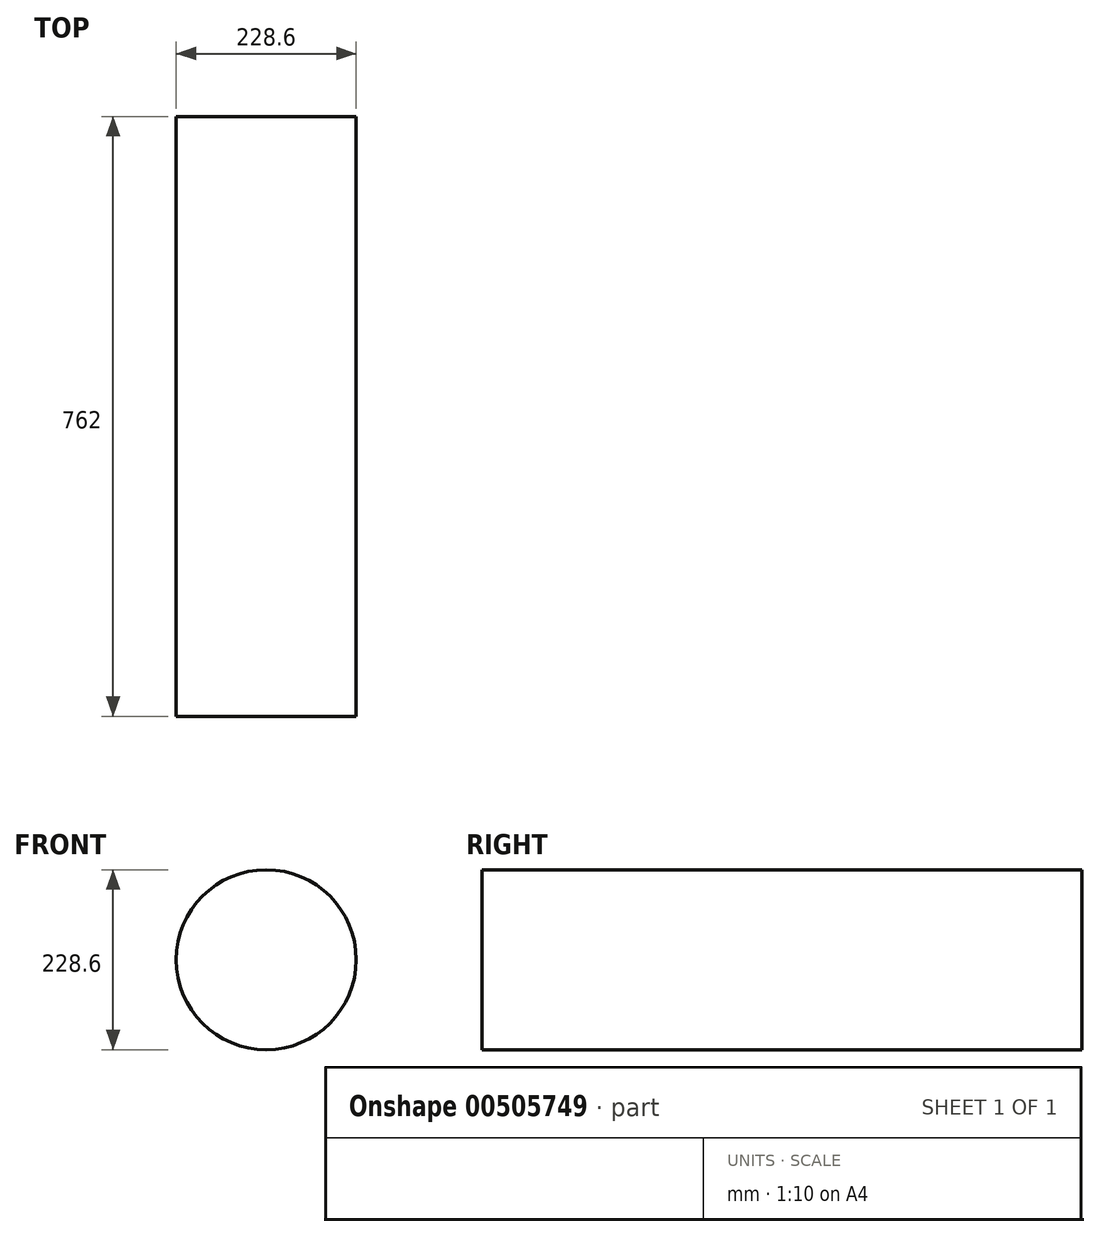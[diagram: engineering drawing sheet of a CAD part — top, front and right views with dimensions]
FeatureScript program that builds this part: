
annotation { "Feature Type Name" : "Feature", "Feature Type Description" : "" }
export const myFeature = defineFeature(function(context is Context, id is Id, definition is map)
    precondition{}
    {
        {
            var Q0;
            Q0=qCreatedBy(makeId("Top.planeOp"),FACE);
            var sketch = newSketch(context, id + "F0", { "sketchPlane" : qUnion([Q0])});
            skLineSegment(sketch, "E0.left", {"start": v(-1447.8, 381) * mm, "end": v(-1447.8, -381) * mm});
            skPoint(sketch, "E0.middle", {"position": v(0, 0) * mm});
            skLineSegment(sketch, "E1.left", {"start": v(-114.3, 381) * mm, "end": v(-114.3, -381) * mm});
            skLineSegment(sketch, "E2.bottom", {"start": v(-1441.45, 381) * mm, "end": v(-1428.75, 381) * mm});
            skLineSegment(sketch, "E2.top", {"start": v(-1441.45, -381) * mm, "end": v(-1428.75, -381) * mm});
            skLineSegment(sketch, "E2.left", {"start": v(-1447.8, 374.65) * mm, "end": v(-1447.8, -374.65) * mm});
            skLineSegment(sketch, "E2.right", {"start": v(-1428.75, 381) * mm, "end": v(-1428.75, -381) * mm});
            skLineSegment(sketch, "E3.bottom", {"start": v(-1428.75, 381) * mm, "end": v(-1162.05, 381) * mm});
            skLineSegment(sketch, "E3.top", {"start": v(-1428.75, -381) * mm, "end": v(-1162.05, -381) * mm});
            skLineSegment(sketch, "E3.right", {"start": v(-1162.05, 381) * mm, "end": v(-1162.05, -381) * mm});
            skLineSegment(sketch, "E4.bottom", {"start": v(-1162.05, 381) * mm, "end": v(-1143, 381) * mm});
            skLineSegment(sketch, "E4.top", {"start": v(-1162.05, -381) * mm, "end": v(-1143, -381) * mm});
            skLineSegment(sketch, "E4.right", {"start": v(-1143, 381) * mm, "end": v(-1143, -381) * mm});
            skLineSegment(sketch, "E5.right", {"start": v(-876.3, 381) * mm, "end": v(-876.3, -381) * mm});
            skLineSegment(sketch, "E6.right", {"start": v(-857.25, 381) * mm, "end": v(-857.25, -381) * mm});
            skLineSegment(sketch, "E7.right", {"start": v(-590.55, 381) * mm, "end": v(-590.55, -381) * mm});
            skLineSegment(sketch, "E8.right", {"start": v(-571.5, 381) * mm, "end": v(-571.5, -381) * mm});
            skLineSegment(sketch, "E9.right", {"start": v(-304.8, 381) * mm, "end": v(-304.8, -381) * mm});
            skLineSegment(sketch, "E10.right", {"start": v(-285.75, 381) * mm, "end": v(-285.75, -381) * mm});
            skPoint(sketch, "E11.visualSharp", {"position": v(-1447.8, 381) * mm});
            skArc(sketch, "E11.filletArc", {"start": v(-1441.45, 381) * mm, "mid": v(-1445.94, 379.14) * mm, "end": v(-1447.8, 374.65) * mm});
            skPoint(sketch, "E12.visualSharp", {"position": v(-1447.8, -381) * mm});
            skArc(sketch, "E12.filletArc", {"start": v(-1447.8, -374.65) * mm, "mid": v(-1445.94, -379.14) * mm, "end": v(-1441.45, -381) * mm});
            skLineSegment(sketch, "E13", {"start": v(0, 381) * mm, "end": v(0, -381) * mm});
            skLineSegment(sketch, "E14", {"start": v(-1447.8, 0) * mm, "end": v(0, 0) * mm});
            skLineSegment(sketch, "E15", {"start": v(-1447.8, 381) * mm, "end": v(0, 381) * mm});
            skLineSegment(sketch, "E16", {"start": v(0, -381) * mm, "end": v(-1447.8, -381) * mm});
            skLineSegment(sketch, "E17.MirrorCS", {"start": v(1441.45, 381) * mm, "end": v(1428.75, 381) * mm});
            skLineSegment(sketch, "E18.MirrorCS", {"start": v(1441.45, -381) * mm, "end": v(1428.75, -381) * mm});
            skArc(sketch, "E19.MirrorCS", {"start": v(1447.8, -374.65) * mm, "mid": v(1445.94, -379.14) * mm, "end": v(1441.45, -381) * mm});
            skArc(sketch, "E20.MirrorCS", {"start": v(1441.45, 381) * mm, "mid": v(1445.94, 379.14) * mm, "end": v(1447.8, 374.65) * mm});
            skLineSegment(sketch, "E21.MirrorCS", {"start": v(1162.05, 381) * mm, "end": v(1143, 381) * mm});
            skLineSegment(sketch, "E22.MirrorCS", {"start": v(1162.05, -381) * mm, "end": v(1143, -381) * mm});
            skLineSegment(sketch, "E23.MirrorCS", {"start": v(1428.75, 381) * mm, "end": v(1162.05, 381) * mm});
            skLineSegment(sketch, "E24.MirrorCS", {"start": v(876.3, 381) * mm, "end": v(876.3, -381) * mm});
            skLineSegment(sketch, "E25.MirrorCS", {"start": v(1447.8, 381) * mm, "end": v(1447.8, -381) * mm});
            skLineSegment(sketch, "E26.MirrorCS", {"start": v(857.25, 381) * mm, "end": v(857.25, -381) * mm});
            skLineSegment(sketch, "E27.MirrorCS", {"start": v(304.8, 381) * mm, "end": v(304.8, -381) * mm});
            skLineSegment(sketch, "E28.MirrorCS", {"start": v(571.5, 381) * mm, "end": v(571.5, -381) * mm});
            skLineSegment(sketch, "E29.MirrorCS", {"start": v(1143, 381) * mm, "end": v(1143, -381) * mm});
            skLineSegment(sketch, "E30.MirrorCS", {"start": v(1428.75, 381) * mm, "end": v(1428.75, -381) * mm});
            skLineSegment(sketch, "E31.MirrorCS", {"start": v(590.55, 381) * mm, "end": v(590.55, -381) * mm});
            skLineSegment(sketch, "E32.MirrorCS", {"start": v(1162.05, 381) * mm, "end": v(1162.05, -381) * mm});
            skLineSegment(sketch, "E33.MirrorCS", {"start": v(1428.75, -381) * mm, "end": v(1162.05, -381) * mm});
            skPoint(sketch, "E34.MirrorP", {"position": v(1447.8, -381) * mm});
            skLineSegment(sketch, "E35.MirrorCS", {"start": v(1447.8, 374.65) * mm, "end": v(1447.8, -374.65) * mm});
            skLineSegment(sketch, "E36.MirrorCS", {"start": v(0, -381) * mm, "end": v(1447.8, -381) * mm});
            skLineSegment(sketch, "E37.MirrorCS", {"start": v(114.3, 381) * mm, "end": v(114.3, -381) * mm});
            skLineSegment(sketch, "E38.MirrorCS", {"start": v(1447.8, 381) * mm, "end": v(0, 381) * mm});
            skPoint(sketch, "E39.MirrorP", {"position": v(1447.8, 381) * mm});
            skLineSegment(sketch, "E40.MirrorCS", {"start": v(285.75, 381) * mm, "end": v(285.75, -381) * mm});
            skLineSegment(sketch, "E41.MirrorCS", {"start": v(1447.8, 0) * mm, "end": v(0, 0) * mm});
            skSolve(sketch);
        }
        {
            var Q0;
            {var subQ0=sQuery(id+"F0.wireOp",EDGE,"E38.MirrorCS");var subQ5=sQuery(id+"F0.wireOp",EDGE,"E37.MirrorCS");var subQ6=makeQuery(id+"F0.imprint","INTERSECT",VERTEX,{"derivedFrom":[subQ5,subQ0]});Q0=makeQuery(id+"F0.imprint","IMPRINT",FACE,{"disambiguationData":[TD([[makeQuery(id+"F0.imprint","IMPRINT",EDGE,{"disambiguationData":[TD([[subQ6,-1.0]])],"derivedFrom":subQ5}),-1.0]])]});}
            var Q1;
            {var subQ0=sQuery(id+"F0.wireOp",EDGE,"E36.MirrorCS");var subQ5=sQuery(id+"F0.wireOp",EDGE,"E37.MirrorCS");var subQ6=makeQuery(id+"F0.imprint","INTERSECT",VERTEX,{"derivedFrom":[subQ0,subQ5]});Q1=makeQuery(id+"F0.imprint","IMPRINT",FACE,{"disambiguationData":[TD([[makeQuery(id+"F0.imprint","IMPRINT",EDGE,{"disambiguationData":[TD([[subQ6,1.0]])],"derivedFrom":subQ5}),-1.0]])]});}
            var Q2;
            Q2=sQuery(id+"F0.wireOp",EDGE,"E13");
            revolve(context, id + "F1", {"entities" : qUnion([Q0, Q1]), "axis" : qUnion([Q2]), "revolveType" : RevolveType.FULL});
        }
        {
            var Q0;
            Q0=qCreatedBy(makeId("Right.planeOp"),FACE);
            var sketch = newSketch(context, id + "F2", { "sketchPlane" : qUnion([Q0])});
            skPoint(sketch, "E42.middle", {"position": v(0, 0) * mm});
            skFitSpline(sketch, "E43", {"points": [v(-381, 0) * mm, v(-274.29, 21.54) * mm], "startDerivative": vector(98.59, 95.62) * mm, "endDerivative": vector(123.75, 0) * mm});
            skFitSpline(sketch, "E44", {"points": [v(-274.29, 21.54) * mm, v(381, 0) * mm], "startDerivative": vector(655.29, -21.54) * mm, "endDerivative": vector(655.29, -21.54) * mm});
            skFitSpline(sketch, "E45", {"points": [v(-381, 0) * mm, v(0, -21.54) * mm, v(381, 0) * mm], "startDerivative": vector(-36.35, -268.14) * mm, "endDerivative": vector(762, 64.62) * mm});
            skSolve(sketch);
        }
        {
            var Q0;
            Q0=sQuery(id+"F2.wireOp",EDGE,"E43");
            var Q1;
            Q1=sQuery(id+"F2.wireOp",EDGE,"E44");
            var Q2;
            Q2=sQuery(id+"F2.wireOp",EDGE,"E45");
            extrude(context, id + "F3", {"bodyType" : ToolBodyType.SURFACE, "surfaceEntities" : qUnion([Q0, Q1, Q2]), "depth" : 19.05 * mm});
        }
    });
